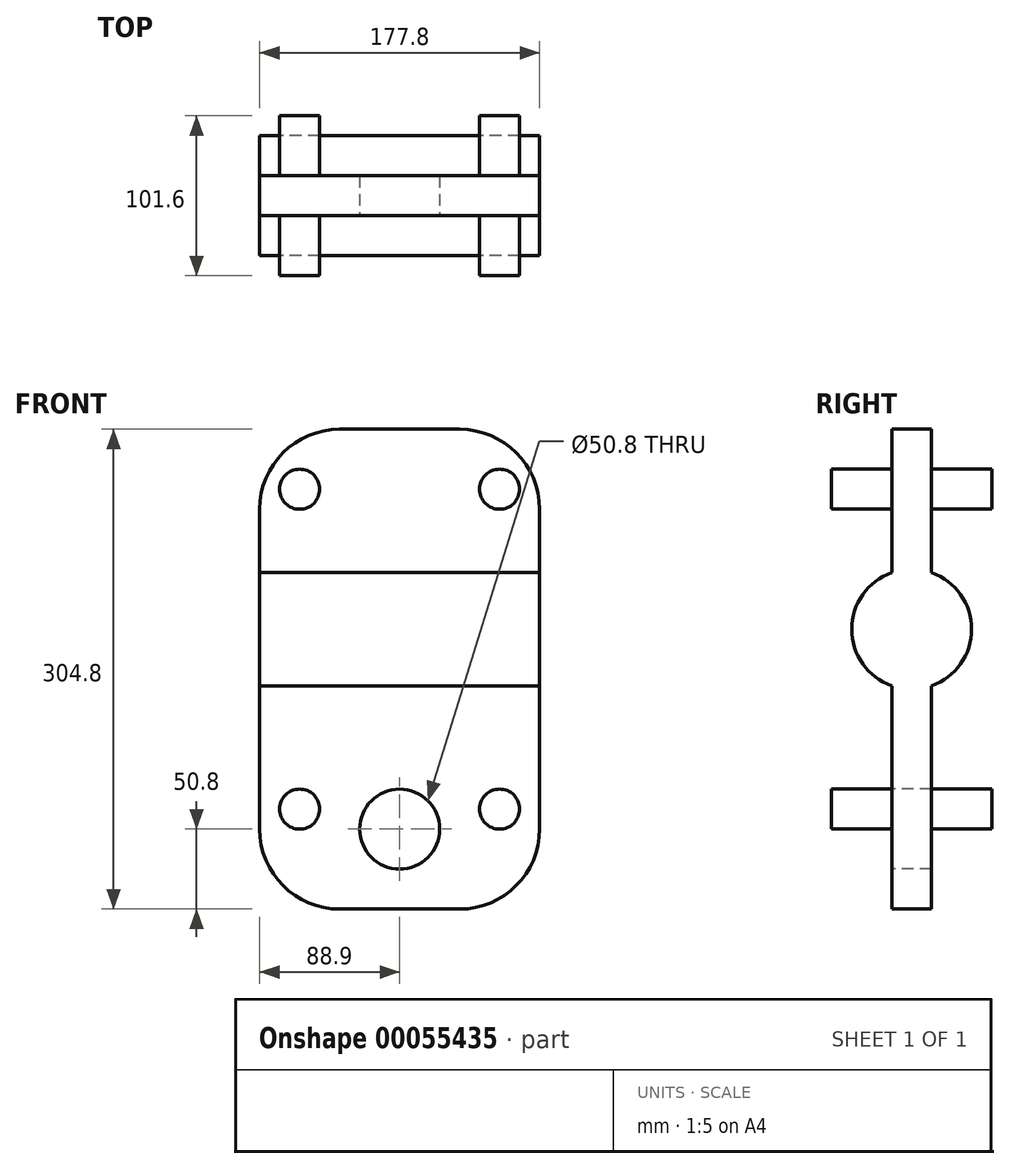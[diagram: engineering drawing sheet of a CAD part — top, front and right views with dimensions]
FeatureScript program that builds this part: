
annotation { "Feature Type Name" : "Feature", "Feature Type Description" : "" }
export const myFeature = defineFeature(function(context is Context, id is Id, definition is map)
    precondition{}
    {
        {
            var Q0;
            Q0=qCreatedBy(makeId("Right.planeOp"),FACE);
            var sketch = newSketch(context, id + "F0", { "sketchPlane" : qUnion([Q0])});
            skCircle(sketch, "E0", {"center": v(0, 0) * mm, "radius": 38.1 * mm});
            skLineSegment(sketch, "E1.rect.bottom", {"start": v(12.7, 127) * mm, "end": v(-12.7, 127) * mm});
            skLineSegment(sketch, "E1.rect.left", {"start": v(12.7, 127) * mm, "end": v(12.7, -127) * mm});
            skLineSegment(sketch, "E1.rect.right", {"start": v(-12.7, 127) * mm, "end": v(-12.7, -127) * mm});
            skLineSegment(sketch, "E2.bottom", {"start": v(12.7, -127) * mm, "end": v(-12.7, -127) * mm});
            skLineSegment(sketch, "E2.top", {"start": v(12.7, -177.8) * mm, "end": v(-12.7, -177.8) * mm});
            skLineSegment(sketch, "E2.left", {"start": v(12.7, -127) * mm, "end": v(12.7, -177.8) * mm});
            skLineSegment(sketch, "E2.right", {"start": v(-12.7, -127) * mm, "end": v(-12.7, -177.8) * mm});
            skSolve(sketch);
        }
        {
            var Q0;
            Q0 = qSketchRegion(id + "F0", true);
            extrude(context, id + "F1", {"entities" : qUnion([Q0]), "depth" : 177.8 * mm});
        }
        {
            var Q0;
            {var subQ0=sQuery(id+"F0.wireOp",EDGE,"E1.rect.left");Q0=makeQuery(id+"F1.opExtrude","SWEPT_FACE",FACE,{"disambiguationData":[OSD([subQ0]),TDD([makeQuery(id+"F0.imprint","IMPRINT",EDGE,{"disambiguationData":[TD([[makeQuery(id+"F0.imprint","INTERSECT",VERTEX,{"derivedFrom":[sQuery(id+"F0.wireOp",EDGE,"E1.rect.bottom"),subQ0]}),-1.0]])],"derivedFrom":subQ0})])]});}
            var sketch = newSketch(context, id + "F2", { "sketchPlane" : qUnion([Q0])});
            skCircle(sketch, "E3", {"center": v(-152.4, 88.9) * mm, "radius": 12.7 * mm});
            skCircle(sketch, "E4", {"center": v(-25.4, 88.9) * mm, "radius": 12.7 * mm});
            skCircle(sketch, "E5", {"center": v(-25.4, -114.3) * mm, "radius": 12.7 * mm});
            skCircle(sketch, "E6", {"center": v(-152.4, -114.3) * mm, "radius": 12.7 * mm});
            skSolve(sketch);
        }
        {
            var Q0;
            Q0 = qSketchRegion(id + "F2", true);
            extrude(context, id + "F3", {"entities" : qUnion([Q0]), "operationType" : NewBodyOperationType.ADD, "depth" : 38.1 * mm});
        }
        {
            var Q0;
            Q0=makeQuery(id+"F1.opExtrude","SWEPT_BODY",BODY,{"disambiguationData":[OSD([sQuery(id+"F0.wireOp",EDGE,"E0"),sQuery(id+"F0.wireOp",EDGE,"E1.rect.bottom"),sQuery(id+"F0.wireOp",EDGE,"E1.rect.top"),sQuery(id+"F0.wireOp",EDGE,"E1.rect.left"),sQuery(id+"F0.wireOp",EDGE,"E1.rect.right")])]});
            var Q1;
            Q1=qCreatedBy(makeId("Front.planeOp"),FACE);
            mirror(context, id + "F4", {"operationType" : NewBodyOperationType.ADD, "entities" : qUnion([Q0]), "mirrorPlane" : qUnion([Q1])});
        }
        {
            var Q0;
            Q0=makeQuery(id+"F1.opExtrude","CAP_EDGE",EDGE,{"disambiguationData":[OSD([sQuery(id+"F0.wireOp",EDGE,"E1.rect.bottom")])],"isStart":false});
            var Q1;
            Q1=makeQuery(id+"F1.opExtrude","CAP_EDGE",EDGE,{"disambiguationData":[OSD([sQuery(id+"F0.wireOp",EDGE,"E1.rect.bottom")])],"isStart":true});
            fillet(context, id + "F5", {"entities" : qUnion([Q0, Q1]), "radius" : 50.8 * mm, "tangentPropagation" : true, "allowEdgeOverflow" : false});
        }
        {
            var Q0;
            {var subQ0=sQuery(id+"F0.wireOp",EDGE,"E1.rect.left");Q0=makeQuery(id+"F1.opExtrude","SWEPT_FACE",FACE,{"disambiguationData":[OSD([subQ0]),TDD([makeQuery(id+"F0.imprint","IMPRINT",EDGE,{"disambiguationData":[TD([[makeQuery(id+"F0.imprint","INTERSECT",VERTEX,{"derivedFrom":[sQuery(id+"F0.wireOp",EDGE,"E1.rect.top"),subQ0]}),1.0]])],"derivedFrom":subQ0})])]});}
            var sketch = newSketch(context, id + "F6", { "sketchPlane" : qUnion([Q0])});
            skCircle(sketch, "E7", {"center": v(-88.9, -127) * mm, "radius": 19.05 * mm});
            skSolve(sketch);
        }
        {
            var Q0;
            Q0=sQuery(id+"F6.wireOp",VERTEX,"E7.center");
            var Q1;
            Q1=makeQuery(id+"F1.opExtrude","SWEPT_BODY",BODY,{"disambiguationData":[OSD([sQuery(id+"F0.wireOp",EDGE,"E0"),sQuery(id+"F0.wireOp",EDGE,"E1.rect.bottom"),sQuery(id+"F0.wireOp",EDGE,"E1.rect.top"),sQuery(id+"F0.wireOp",EDGE,"E1.rect.left"),sQuery(id+"F0.wireOp",EDGE,"E1.rect.right")])]});
            hole(context, id + "F7", {"style" : HoleStyle.SIMPLE, "holeDiameter" : 50.8 * mm, "endStyle" : HoleEndStyle.THROUGH, "locations" : qUnion([Q0]), "scope" : qUnion([Q1])});
        }
        {
            var Q0;
            Q0=makeQuery(id+"F1.opExtrude","CAP_EDGE",EDGE,{"disambiguationData":[OSD([sQuery(id+"F0.wireOp",EDGE,"E2.top")])],"isStart":false});
            var Q1;
            Q1=makeQuery(id+"F1.opExtrude","CAP_EDGE",EDGE,{"disambiguationData":[OSD([sQuery(id+"F0.wireOp",EDGE,"E2.top")])],"isStart":true});
            fillet(context, id + "F8", {"entities" : qUnion([Q0, Q1]), "radius" : 50.8 * mm, "tangentPropagation" : true, "allowEdgeOverflow" : false});
        }
    });
